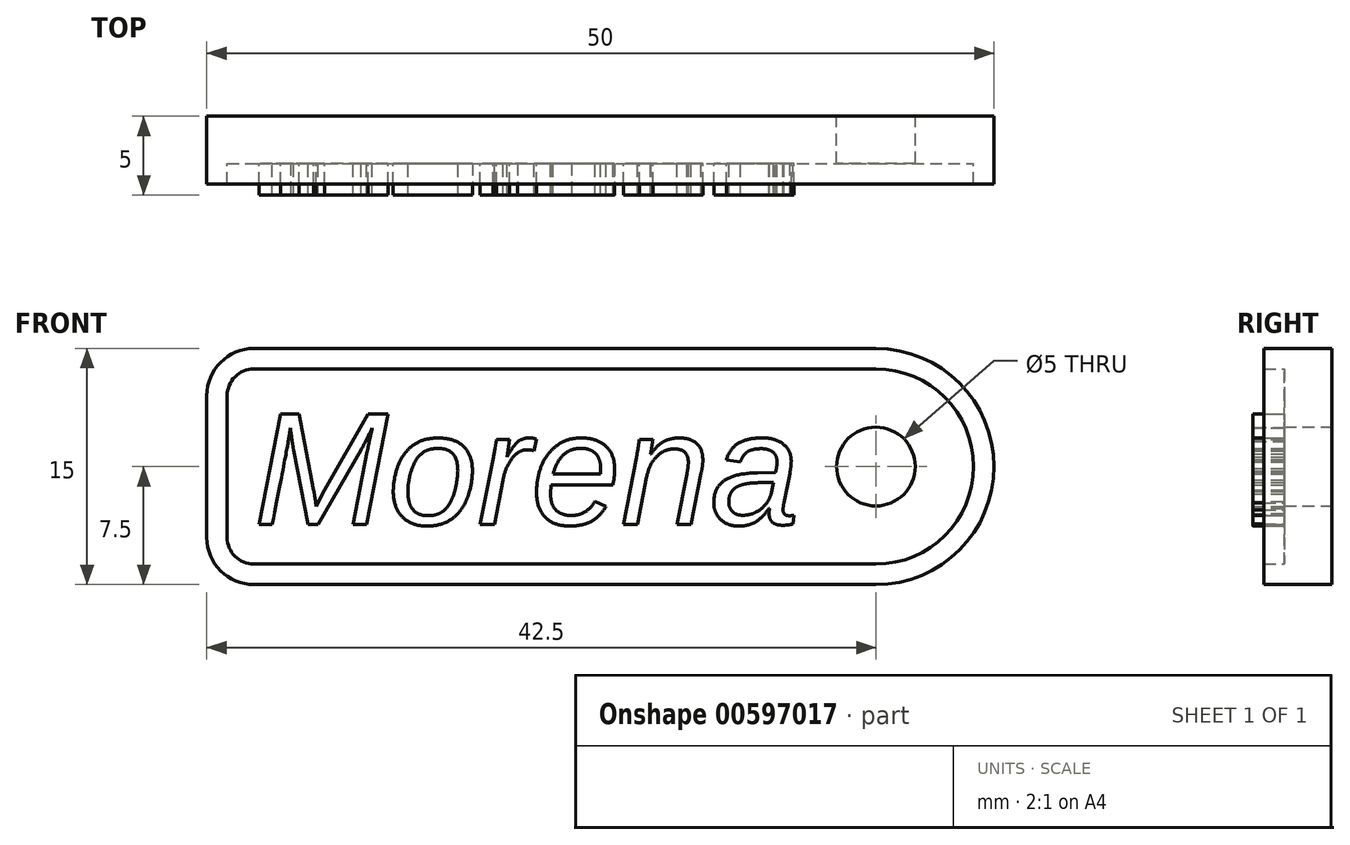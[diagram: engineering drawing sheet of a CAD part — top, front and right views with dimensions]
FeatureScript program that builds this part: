
annotation { "Feature Type Name" : "Feature", "Feature Type Description" : "" }
export const myFeature = defineFeature(function(context is Context, id is Id, definition is map)
    precondition{}
    {
        {
            var Q0;
            Q0=qCreatedBy(makeId("Front.planeOp"),FACE);
            var sketch = newSketch(context, id + "F0", { "sketchPlane" : qUnion([Q0])});
            skLineSegment(sketch, "E0.bottom", {"start": v(-18.25, 7.5) * mm, "end": v(21.25, 7.5) * mm});
            skLineSegment(sketch, "E0.top", {"start": v(-18.25, -7.5) * mm, "end": v(21.25, -7.5) * mm});
            skLineSegment(sketch, "E0.left", {"start": v(-21.25, 4.5) * mm, "end": v(-21.25, -4.5) * mm});
            skPoint(sketch, "E0.middle", {"position": v(0, 0) * mm});
            skArc(sketch, "E1", {"start": v(21.25, -7.5) * mm, "mid": v(28.75, 0) * mm, "end": v(21.25, 7.5) * mm});
            skPoint(sketch, "E2.visualSharp", {"position": v(-21.25, 7.5) * mm});
            skArc(sketch, "E2.filletArc", {"start": v(-18.25, 7.5) * mm, "mid": v(-20.37, 6.62) * mm, "end": v(-21.25, 4.5) * mm});
            skPoint(sketch, "E3.visualSharp", {"position": v(-21.25, -7.5) * mm});
            skArc(sketch, "E3.filletArc", {"start": v(-21.25, -4.5) * mm, "mid": v(-20.37, -6.62) * mm, "end": v(-18.25, -7.5) * mm});
            skCircle(sketch, "E4", {"center": v(21.25, 0) * mm, "radius": 2.5 * mm});
            skSolve(sketch);
        }
        {
            var Q0;
            Q0=makeQuery(id+"F0.imprint","IMPRINT",FACE,{"disambiguationData":[TD([[makeQuery(id+"F0.imprint","IMPRINT",EDGE,{"derivedFrom":sQuery(id+"F0.wireOp",EDGE,"E0.bottom")}),-1.0]])]});
            extrude(context, id + "F1", {"entities" : qUnion([Q0]), "depth" : 3 * mm, "offsetDistance" : 25 * mm});
        }
        {
            var Q0;
            Q0=makeQuery(id+"F1.opExtrude","CAP_FACE",FACE,{"disambiguationData":[OSD([sQuery(id+"F0.wireOp",EDGE,"E0.bottom"),sQuery(id+"F0.wireOp",EDGE,"E0.top"),sQuery(id+"F0.wireOp",EDGE,"E0.left"),sQuery(id+"F0.wireOp",EDGE,"E1"),sQuery(id+"F0.wireOp",EDGE,"E2.filletArc"),sQuery(id+"F0.wireOp",EDGE,"E3.filletArc"),sQuery(id+"F0.wireOp",EDGE,"E4")])],"isStart":false});
            var sketch = newSketch(context, id + "F2", { "sketchPlane" : qUnion([Q0])});
            skText(sketch, "E5", { "text": "Morena", "fontName": "Arimo-Italic.ttf"});
            const initialGuessF2  = {"E5": [-0.01825, -0.00368, 1, 0, 0.00736]};
            skSetInitialGuess(sketch, initialGuessF2);
            skSolve(sketch);
        }
        {
            var Q0;
            Q0 = qSketchRegion(id + "F2", true);
            extrude(context, id + "F3", {"entities" : qUnion([Q0]), "operationType" : NewBodyOperationType.ADD, "depth" : 2 * mm, "offsetDistance" : 25 * mm});
        }
        {
            var Q0;
            {var subQ0=sQuery(id+"F0.wireOp",EDGE,"E0.left");var subQ1=sQuery(id+"F0.wireOp",EDGE,"E0.top");var subQ2=sQuery(id+"F0.wireOp",EDGE,"E1");var subQ3=sQuery(id+"F0.wireOp",EDGE,"E2.filletArc");var subQ4=sQuery(id+"F0.wireOp",EDGE,"E0.bottom");var subQ5=sQuery(id+"F0.wireOp",EDGE,"E3.filletArc");var subQ6=sQuery(id+"F0.wireOp",EDGE,"E4");Q0=makeQuery(id+"F3.boolean.opBoolean","SPLIT",FACE,{"disambiguationData":[TD([makeQuery(id+"F1.opExtrude","SWEPT_FACE",FACE,{"disambiguationData":[OSD([subQ4])]})])],"derivedFrom":makeQuery(id+"F1.opExtrude","CAP_FACE",FACE,{"disambiguationData":[OSD([subQ4,subQ1,subQ0,subQ2,subQ3,subQ5,subQ6])],"isStart":false})});}
            var sketch = newSketch(context, id + "F4", { "sketchPlane" : qUnion([Q0])});
            skArc(sketch, "E6.0", {"start": v(-18.25, 6.2) * mm, "mid": v(-19.45, 5.7) * mm, "end": v(-19.95, 4.5) * mm});
            skArc(sketch, "E6.1", {"start": v(-19.95, -4.5) * mm, "mid": v(-19.45, -5.7) * mm, "end": v(-18.25, -6.2) * mm});
            skLineSegment(sketch, "E6.2", {"start": v(-18.25, -6.2) * mm, "end": v(21.25, -6.2) * mm});
            skLineSegment(sketch, "E6.3", {"start": v(-19.95, 4.5) * mm, "end": v(-19.95, -4.5) * mm});
            skArc(sketch, "E6.4", {"start": v(21.25, -6.2) * mm, "mid": v(27.45, 0) * mm, "end": v(21.25, 6.2) * mm});
            skLineSegment(sketch, "E6.5", {"start": v(21.25, 6.2) * mm, "end": v(-18.25, 6.2) * mm});
            skCircle(sketch, "E7.0", {"center": v(21.25, 0) * mm, "radius": 3.6 * mm});
            skSolve(sketch);
        }
        {
            var Q0;
            Q0=makeQuery(id+"F4.imprint","IMPRINT",FACE,{"disambiguationData":[TD([[makeQuery(id+"F4.imprint","IMPRINT",EDGE,{"derivedFrom":sQuery(id+"F4.wireOp",EDGE,"E6.0")}),-1.0]])]});
            extrude(context, id + "F5", {"entities" : qUnion([Q0]), "operationType" : NewBodyOperationType.ADD, "depth" : 1.3 * mm, "offsetDistance" : 25 * mm});
        }
    });
